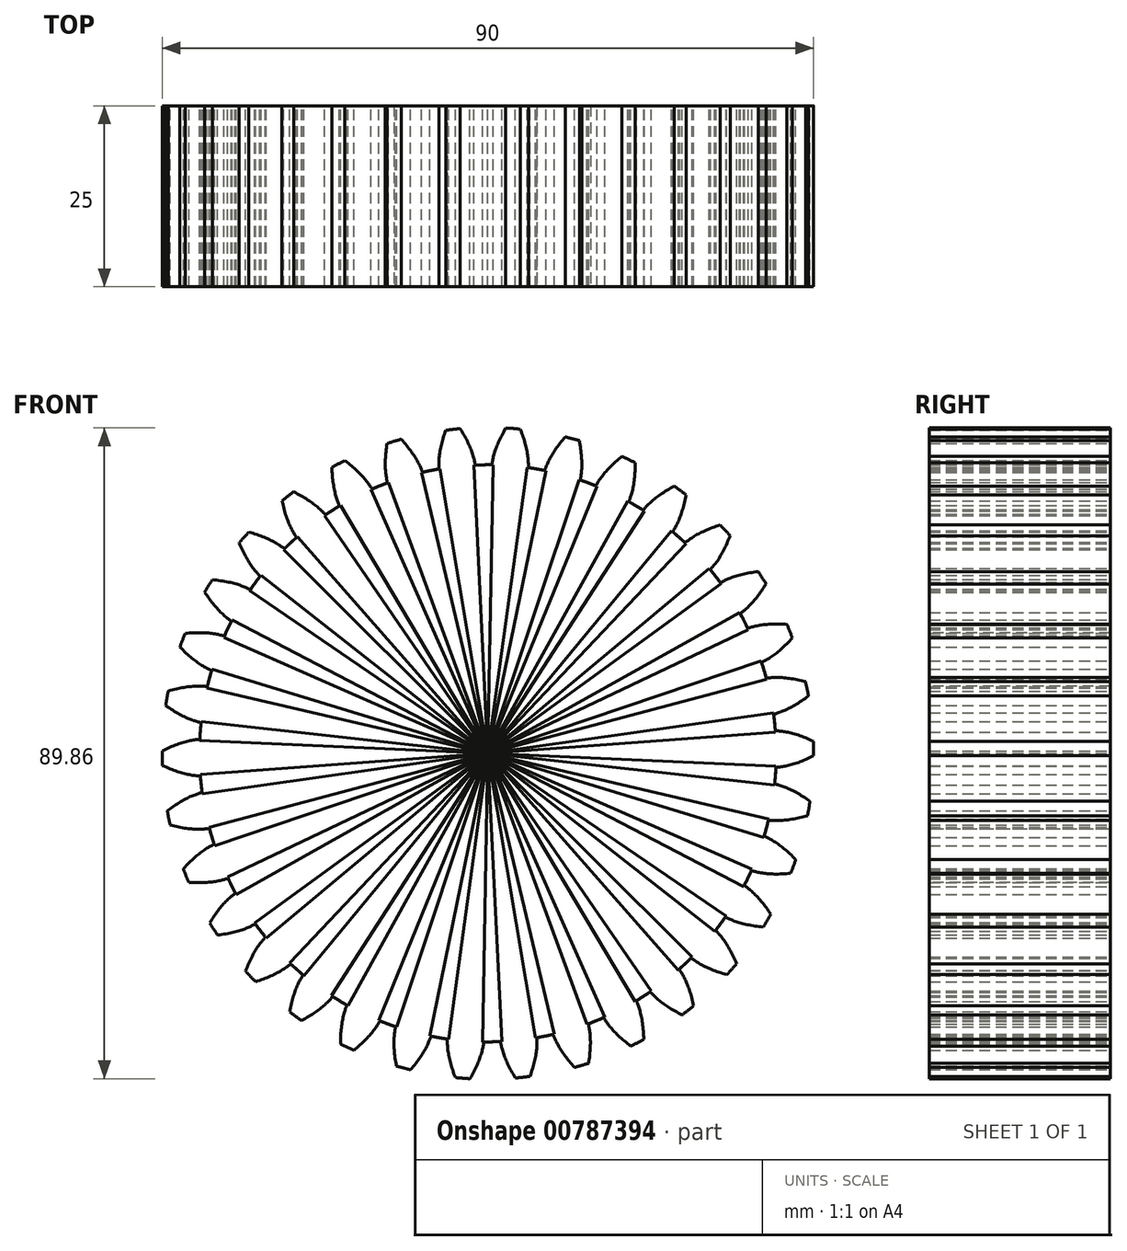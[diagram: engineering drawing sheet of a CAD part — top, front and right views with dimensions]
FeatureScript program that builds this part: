
annotation { "Feature Type Name" : "Feature", "Feature Type Description" : "" }
export const myFeature = defineFeature(function(context is Context, id is Id, definition is map)
    precondition{}
    {
        {
            var Q0;
            Q0=qCreatedBy(makeId("Front.planeOp"),FACE);
            var sketch = newSketch(context, id + "F0", { "sketchPlane" : qUnion([Q0])});
            skArc(sketch, "E0", {"start": v(-3.8, 44.84) * mm, "mid": v(-4.82, 44.74) * mm, "end": v(-5.83, 44.62) * mm});
            skArc(sketch, "E1", {"start": v(0.73, 39.84) * mm, "mid": v(-0.51, 39.85) * mm, "end": v(-1.76, 39.81) * mm});
            skFitSpline(sketch, "E2", {"points": [v(-6.78, 39.4) * mm, v(-6.79, 39.65) * mm, v(-6.78, 40.16) * mm, v(-6.73, 40.92) * mm, v(-6.58, 41.93) * mm, v(-6.29, 43.16) * mm, v(-5.83, 44.62) * mm], "startDerivative": vector(-0.27, 2.54) * mm, "endDerivative": vector(2.17, 6.53) * mm});
            skLineSegment(sketch, "E3", {"start": v(0, 0) * mm, "end": v(-9.2, 38.77) * mm});
            skLineSegment(sketch, "E4", {"start": v(-6.76, 39.27) * mm, "end": v(-6.78, 39.4) * mm});
            skLineSegment(sketch, "E5.MirrorCS", {"start": v(-1.76, 39.81) * mm, "end": v(-1.77, 39.93) * mm});
            skLineSegment(sketch, "E6.MirrorCS", {"start": v(0, 0) * mm, "end": v(0.73, 39.84) * mm});
            skFitSpline(sketch, "E7.MirrorCS", {"points": [v(-1.77, 39.93) * mm, v(-1.81, 40.18) * mm, v(-1.92, 40.68) * mm, v(-2.14, 41.41) * mm, v(-2.5, 42.36) * mm, v(-3.05, 43.51) * mm, v(-3.8, 44.84) * mm], "startDerivative": vector(-0.28, 2.54) * mm, "endDerivative": vector(-3.51, 5.92) * mm});
            skArc(sketch, "E8.trimOffspring", {"start": v(-6.76, 39.27) * mm, "mid": v(-7.98, 39.04) * mm, "end": v(-9.2, 38.77) * mm});
            skSolve(sketch);
        }
        {
            var Q0;
            Q0=makeQuery(id+"F0.imprint","IMPRINT",FACE,{"disambiguationData":[TD([[makeQuery(id+"F0.imprint","IMPRINT",EDGE,{"derivedFrom":sQuery(id+"F0.wireOp",EDGE,"E0")}),1.0]])]});
            extrude(context, id + "F1", {"entities" : qUnion([Q0]), "depth" : 25 * mm, "offsetDistance" : 25 * mm});
        }
        {
            var Q0;
            Q0=makeQuery(id+"F1.opExtrude","SWEPT_EDGE",EDGE,{"disambiguationData":[OSD([sQuery(id+"F0.wireOp",EDGE,"E1"),sQuery(id+"F0.wireOp",EDGE,"E5.MirrorCS")])]});
            var Q1;
            Q1=makeQuery(id+"F1.opExtrude","SWEPT_EDGE",EDGE,{"disambiguationData":[OSD([sQuery(id+"F0.wireOp",EDGE,"E4"),sQuery(id+"F0.wireOp",EDGE,"E8.trimOffspring")])]});
            fillet(context, id + "F2", {"entities" : qUnion([Q0, Q1]), "radius" : 0.2 * mm, "tangentPropagation" : true, "allowEdgeOverflow" : false});
        }
        {
            var Q0;
            Q0=makeQuery(id+"F1.opExtrude","SWEPT_BODY",BODY,{"disambiguationData":[OSD([sQuery(id+"F0.wireOp",EDGE,"E0"),sQuery(id+"F0.wireOp",EDGE,"E1"),sQuery(id+"F0.wireOp",EDGE,"E2"),sQuery(id+"F0.wireOp",EDGE,"E3"),sQuery(id+"F0.wireOp",EDGE,"E4"),sQuery(id+"F0.wireOp",EDGE,"E5.MirrorCS"),sQuery(id+"F0.wireOp",EDGE,"E6.MirrorCS"),sQuery(id+"F0.wireOp",EDGE,"E7.MirrorCS"),sQuery(id+"F0.wireOp",EDGE,"E8.trimOffspring")])]});
            var Q1;
            Q1=makeQuery(id+"F1.opExtrude","SWEPT_EDGE",EDGE,{"disambiguationData":[OSD([sQuery(id+"F0.wireOp",EDGE,"E3"),sQuery(id+"F0.wireOp",EDGE,"E6.MirrorCS")])]});
            circularPattern(context, id + "F3", {"entities" : qUnion([Q0]), "axis" : qUnion([Q1]), "angle" : 360 * degree, "instanceCount" : 34, "equalSpace" : true});
        }
    });
